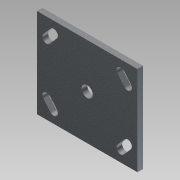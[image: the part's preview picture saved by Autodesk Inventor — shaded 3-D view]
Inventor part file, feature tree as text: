
AUTODESK INVENTOR PART (.ipt)
format: ipt  version: 2013 (Build 170138000, 138)  size: 133,120 bytes
history: native  units: in
note: dims shown in document units (in); Inventor stores cm internally (conversion verified against a paired STEP export)
features: extrude x2, sketch x2
ambient origin geometry x8: Origin, YZ Plane, XZ Plane, XY Plane, X Axis, Y Axis, Z Axis, Center Point
bodies: Solid1 (feature_tree)
feature tree (4):
  extrude  "Extrusion1"  Depth=4.0in
  extrude  "Extrusion2"  Depth=0.375in
  sketch  "Sketch1"  dims[d0=4.5in d1=4.0in]
  sketch  "Sketch2"  dims[d8=0.375in d9=0.375in d10=0.375in d11=1.8125in d14=1.8125in d16=0.375in d20=0.375in d22=0.375in d23=0.25in d24=0.0in d25=0.5in d26=0.25in d27=0.0in]
